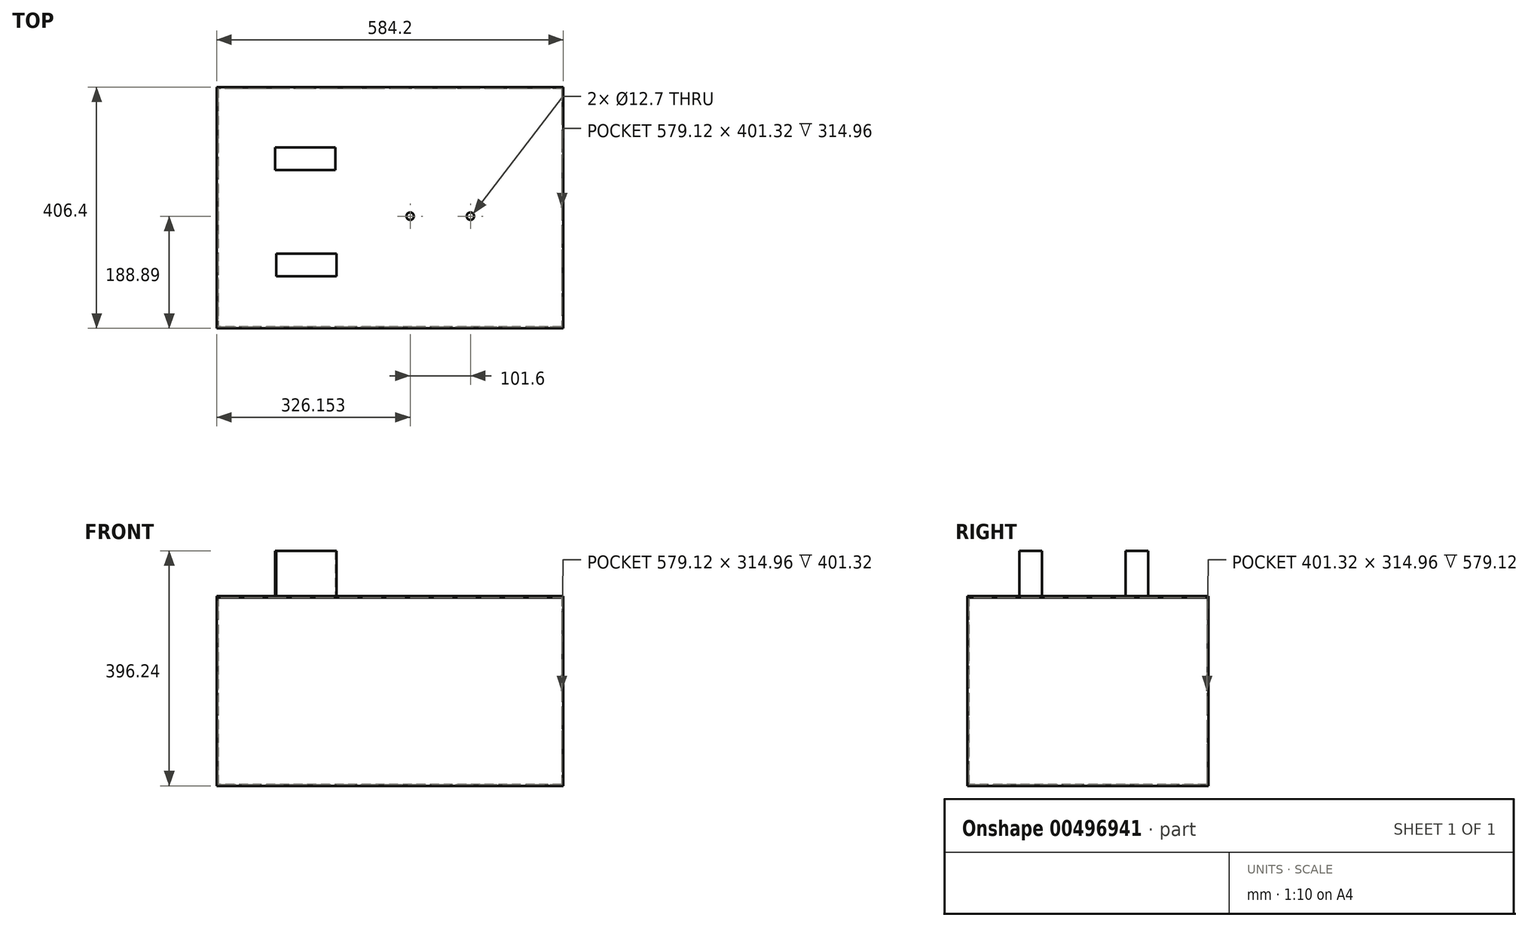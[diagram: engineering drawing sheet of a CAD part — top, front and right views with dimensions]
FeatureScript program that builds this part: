
annotation { "Feature Type Name" : "Feature", "Feature Type Description" : "" }
export const myFeature = defineFeature(function(context is Context, id is Id, definition is map)
    precondition{}
    {
        {
            var Q0;
            Q0=qCreatedBy(makeId("Top.planeOp"),FACE);
            var sketch = newSketch(context, id + "F0", { "sketchPlane" : qUnion([Q0])});
            skLineSegment(sketch, "E0.bottom", {"start": v(214, 217.5) * mm, "end": v(-370.2, 217.5) * mm});
            skLineSegment(sketch, "E0.top", {"start": v(214, -188.9) * mm, "end": v(-370.2, -188.9) * mm});
            skLineSegment(sketch, "E0.left", {"start": v(214, 217.5) * mm, "end": v(214, -188.9) * mm});
            skLineSegment(sketch, "E0.right", {"start": v(-370.2, 217.5) * mm, "end": v(-370.2, -188.9) * mm});
            skSolve(sketch);
        }
        {
            var Q0;
            Q0=makeQuery(id+"F0.imprint","IMPRINT",FACE,{"disambiguationData":[TD([[makeQuery(id+"F0.imprint","IMPRINT",EDGE,{"derivedFrom":sQuery(id+"F0.wireOp",EDGE,"E0.bottom")}),1.0]])]});
            extrude(context, id + "F1", {"entities" : qUnion([Q0]), "depth" : 317.5 * mm});
        }
        {
            var Q0;
            Q0=makeQuery(id+"F1.opExtrude","CAP_FACE",FACE,{"disambiguationData":[OSD([sQuery(id+"F0.wireOp",EDGE,"E0.bottom"),sQuery(id+"F0.wireOp",EDGE,"E0.top"),sQuery(id+"F0.wireOp",EDGE,"E0.left"),sQuery(id+"F0.wireOp",EDGE,"E0.right")])],"isStart":false});
            shell(context, id + "F2", {"entities" : qUnion([Q0]), "thickness" : 2.54 * mm});
        }
        {
            var Q0;
            Q0=makeQuery(id+"F1.opExtrude","CAP_EDGE",EDGE,{"disambiguationData":[OSD([sQuery(id+"F0.wireOp",EDGE,"E0.left")])],"isStart":false});
            cPoint(context, id + "F3", {"entities" : qUnion([Q0]), "parameter" : 0.5});
        }
        {
            var Q0;
            {var subQ0=sQuery(id+"F0.wireOp",EDGE,"E0.right");Q0=makeQuery(id+"F2.opShell","OFFSET_EDGE",EDGE,{"disambiguationData":[OSD([subQ0]),TDD([makeQuery(id+"F1.opExtrude","CAP_EDGE",EDGE,{"disambiguationData":[OSD([subQ0])],"isStart":false})])]});}
            cPoint(context, id + "F4", {"entities" : qUnion([Q0]), "parameter" : 0.5});
        }
        {
            var Q0;
            {var subQ0=sQuery(id+"F0.wireOp",EDGE,"E0.bottom");Q0=makeQuery(id+"F2.opShell","OFFSET_EDGE",EDGE,{"disambiguationData":[OSD([subQ0]),TDD([makeQuery(id+"F1.opExtrude","CAP_EDGE",EDGE,{"disambiguationData":[OSD([subQ0])],"isStart":false})])]});}
            cPoint(context, id + "F5", {"entities" : qUnion([Q0]), "parameter" : 0.5});
        }
        {
            var Q0;
            Q0 = qCreatedBy(id + "F3" ,VERTEX);
            var Q1;
            Q1 = qCreatedBy(id + "F4" ,VERTEX);
            var Q2;
            Q2 = qCreatedBy(id + "F5" ,VERTEX);
            cPlane(context, id + "F6", {"entities" : qUnion([Q0, Q1, Q2]), "cplaneType" : CPlaneType.THREE_POINT, "offset" : 25.4 * mm, "width" : 152.4 * mm, "height" : 152.4 * mm});
        }
        {
            var Q0;
            Q0=qCreatedBy(id+"F6.planeOp",FACE);
            var sketch = newSketch(context, id + "F7", { "sketchPlane" : qUnion([Q0])});
            skLineSegment(sketch, "E1.bottom", {"start": v(213.88, 217.5) * mm, "end": v(-370.2, 217.5) * mm});
            skLineSegment(sketch, "E1.top", {"start": v(213.88, -188.88) * mm, "end": v(-370.2, -188.88) * mm});
            skLineSegment(sketch, "E1.left", {"start": v(213.88, 217.5) * mm, "end": v(213.88, -188.88) * mm});
            skLineSegment(sketch, "E1.right", {"start": v(-370.2, 217.5) * mm, "end": v(-370.2, -188.88) * mm});
            skSolve(sketch);
        }
        {
            var Q0;
            Q0 = qSketchRegion(id + "F7", true);
            extrude(context, id + "F8", {"entities" : qUnion([Q0]), "operationType" : NewBodyOperationType.ADD, "depth" : 2.54 * mm});
        }
        {
            var Q0;
            Q0=makeQuery(id+"F8.opExtrude","CAP_FACE",FACE,{"disambiguationData":[OSD([sQuery(id+"F7.wireOp",EDGE,"E1.bottom"),sQuery(id+"F7.wireOp",EDGE,"E1.top"),sQuery(id+"F7.wireOp",EDGE,"E1.left"),sQuery(id+"F7.wireOp",EDGE,"E1.right")])],"isStart":false});
            var sketch = newSketch(context, id + "F9", { "sketchPlane" : qUnion([Q0])});
            skCircle(sketch, "E2", {"center": v(-44.05, 0) * mm, "radius": 6.35 * mm});
            skCircle(sketch, "E3", {"center": v(57.55, 0) * mm, "radius": 6.35 * mm});
            skLineSegment(sketch, "E4.bottom", {"start": v(-256.1, 142.43) * mm, "end": v(-148.47, 142.43) * mm});
            skLineSegment(sketch, "E4.top", {"start": v(-256.1, 116.9) * mm, "end": v(-148.47, 116.9) * mm});
            skLineSegment(sketch, "E4.left", {"start": v(-256.1, 142.43) * mm, "end": v(-256.1, 116.9) * mm});
            skLineSegment(sketch, "E4.right", {"start": v(-148.47, 142.43) * mm, "end": v(-148.47, 116.9) * mm});
            skSolve(sketch);
        }
        {
            var Q0;
            Q0=sQuery(id+"F9.wireOp",VERTEX,"E2.center");
            var Q1;
            Q1=sQuery(id+"F9.wireOp",VERTEX,"E3.center");
            var Q2;
            Q2=makeQuery(id+"F1.opExtrude","SWEPT_BODY",BODY,{"disambiguationData":[OSD([sQuery(id+"F0.wireOp",EDGE,"E0.bottom"),sQuery(id+"F0.wireOp",EDGE,"E0.top"),sQuery(id+"F0.wireOp",EDGE,"E0.left"),sQuery(id+"F0.wireOp",EDGE,"E0.right")])]});
            hole(context, id + "F10", {"style" : HoleStyle.SIMPLE, "endStyle" : HoleEndStyle.BLIND, "holeDiameter" : 12.7 * mm, "holeDepth" : 2.54 * mm, "isTappedThrough" : true, "tappedDepth" : 12.7 * mm, "tapClearance" : 3, "locations" : qUnion([Q0, Q1]), "scope" : qUnion([Q2])});
        }
        {
            var Q0;
            Q0=makeQuery(id+"F8.opExtrude","CAP_FACE",FACE,{"disambiguationData":[OSD([sQuery(id+"F7.wireOp",EDGE,"E1.bottom"),sQuery(id+"F7.wireOp",EDGE,"E1.top"),sQuery(id+"F7.wireOp",EDGE,"E1.left"),sQuery(id+"F7.wireOp",EDGE,"E1.right")])],"isStart":false});
            var sketch = newSketch(context, id + "F11", { "sketchPlane" : qUnion([Q0])});
            skLineSegment(sketch, "E5.bottom", {"start": v(-169.93, 115.85) * mm, "end": v(-271.53, 115.85) * mm});
            skLineSegment(sketch, "E5.top", {"start": v(-169.93, 77.75) * mm, "end": v(-271.53, 77.75) * mm});
            skLineSegment(sketch, "E5.left", {"start": v(-169.93, 115.85) * mm, "end": v(-169.93, 77.75) * mm});
            skLineSegment(sketch, "E5.right", {"start": v(-271.53, 115.85) * mm, "end": v(-271.53, 77.75) * mm});
            skLineSegment(sketch, "E6.bottom", {"start": v(-270.17, -101) * mm, "end": v(-168.57, -101) * mm});
            skLineSegment(sketch, "E6.top", {"start": v(-270.17, -62.9) * mm, "end": v(-168.57, -62.9) * mm});
            skLineSegment(sketch, "E6.left", {"start": v(-270.17, -101) * mm, "end": v(-270.17, -62.9) * mm});
            skLineSegment(sketch, "E6.right", {"start": v(-168.57, -101) * mm, "end": v(-168.57, -62.9) * mm});
            skSolve(sketch);
        }
        {
            var Q0;
            Q0=makeQuery(id+"F11.imprint","IMPRINT",FACE,{"disambiguationData":[TD([[makeQuery(id+"F11.imprint","IMPRINT",EDGE,{"derivedFrom":sQuery(id+"F11.wireOp",EDGE,"E5.bottom")}),1.0]])]});
            var Q1;
            Q1=makeQuery(id+"F11.imprint","IMPRINT",FACE,{"disambiguationData":[TD([[makeQuery(id+"F11.imprint","IMPRINT",EDGE,{"derivedFrom":sQuery(id+"F11.wireOp",EDGE,"E6.bottom")}),1.0]])]});
            extrude(context, id + "F12", {"entities" : qUnion([Q0, Q1]), "operationType" : NewBodyOperationType.ADD, "depth" : 76.2 * mm});
        }
    });
